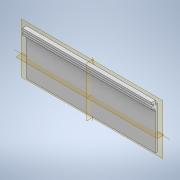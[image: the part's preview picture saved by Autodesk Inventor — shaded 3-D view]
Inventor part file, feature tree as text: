
AUTODESK INVENTOR PART (.ipt)
format: ipt  version: 2022.4 (Build 264492010, 492A)  size: 118,272 bytes
history: native  units: mm
features: extrude x1
ambient origin geometry x8: Origin, YZ Plane, XZ Plane, XY Plane, X Axis, Y Axis, Z Axis, Center Point
bodies: Solid1 (feature_tree)
feature tree (1):
  extrude  "Extrusion1"  Depth=32.5mm
